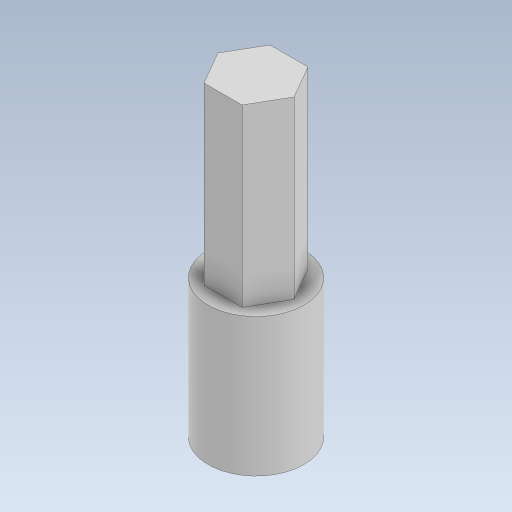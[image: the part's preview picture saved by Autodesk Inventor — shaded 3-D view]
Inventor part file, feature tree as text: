
AUTODESK INVENTOR PART (.ipt)
format: ipt  version: 2023.5 (Build 275446000, 446)  size: 289,792 bytes
history: native  units: mm
features: extrude x6, sketch x4, hole x1
ambient origin geometry x8: Origin, YZ Plane, XZ Plane, XY Plane, X Axis, Y Axis, Z Axis, Center Point
bodies: Solid1 (feature_tree), Solid2 (feature_tree)
feature tree (11):
  extrude  "Extrusion2"  Depth=2.38mm TaperAngle=0.0deg
  extrude  "Extrusion3"  Depth=7.0mm
  extrude  "Extrusion5"  Depth=9.0mm
  extrude  "Extrusion11"  Depth=4.5mm
  extrude  "Extrusion6"  Depth=3.7mm
  hole  "Hole1"  [1 undecoded]
  extrude  "Extrusion1"  Depth=7.16mm
  sketch  "Sketch7"  dims[d0=25.0mm d1=2.38mm d2=0.0mm]
  sketch  "Sketch9"  dims[d3=4.0mm d4=7.0mm]
  sketch  "Sketch10"  dims[d5=3.5mm d6=9.0mm]
  sketch  "Sketch15"  dims[d7=13.0mm d8=0.0mm d9=4.5mm d10=3.7mm d11=13.0mm d12=0.0mm d15=7.16mm d16=16.5mm d17=0.0mm d18=0.5mm d19=0.0mm d21=2.0mm d22=2.25mm d23=0.0mm d24=2.0mm d25=6.0mm d26=4.0mm d27=2.0mm d28=90.0deg d29=3.33mm d30=0.0mm d41=2.0mm d42=4.25mm d43=0.0mm d13=0.5mm d14=0.872665mm d34=0.5mm d35=0.872665mm d36=0.5mm d37=0.872665mm d38=0.5mm d39=0.872665mm d40=0.5mm]
note: 1 required parameter value undecoded (feature->parameter linkage not recoverable at this tier; creation-order binding heuristic only, values carry confidence <= 0.55)
